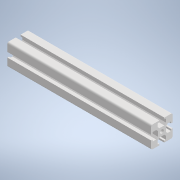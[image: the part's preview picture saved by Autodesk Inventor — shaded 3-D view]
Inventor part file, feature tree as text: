
AUTODESK INVENTOR PART (.ipt)
format: ipt  version: 2021 (Build 250183000, 183)  size: 174,592 bytes
history: native  units: in
note: dims shown in document units (in); Inventor stores cm internally (conversion verified against a paired STEP export)
features: extrude x1, sketch x1
ambient origin geometry x8: Origin, YZ Plane, XZ Plane, XY Plane, X Axis, Y Axis, Z Axis, Center Point
bodies: Solid1 (feature_tree)
feature tree (2):
  extrude  "Extrusion1"  Depth=0.29in
  sketch  "Sketch2"  dims[d9=0.2325in d18=0.055in d20=0.055in d34=0.29in d35=0.055in d37=0.058in d38=0.1225in d39=0.081in d40=135.0deg d41=0.17in d42=0.081in d43=0.058in d44=0.055in d45=0.75in d46=0.055in d47=1.5748in d49=360.0deg d51=0.2348in d52=0.232in d56=0.75in d58=0.125in d61=0.055in d62=0.055in d63=0.055in d64=0.055in d65=1.5748in d67=360.0deg d69=7.125in d70=0.0in d71=0.1225in]
